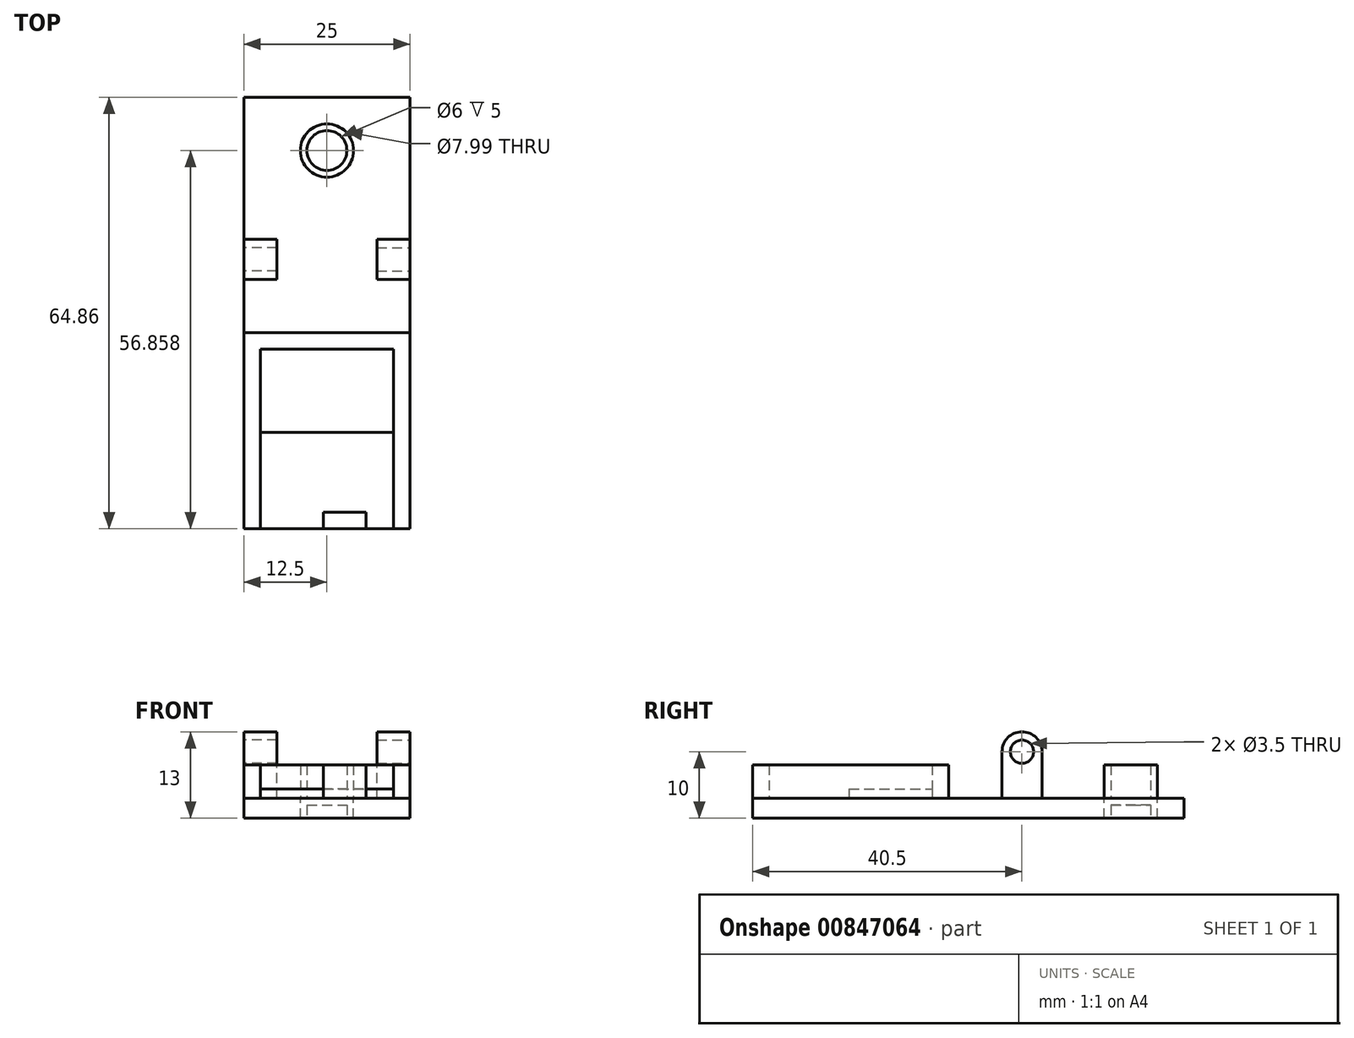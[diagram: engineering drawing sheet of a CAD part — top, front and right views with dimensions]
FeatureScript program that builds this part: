
annotation { "Feature Type Name" : "Feature", "Feature Type Description" : "" }
export const myFeature = defineFeature(function(context is Context, id is Id, definition is map)
    precondition{}
    {
        {
            var Q0;
            Q0=qCreatedBy(makeId("Top.planeOp"),FACE);
            var sketch = newSketch(context, id + "F0", { "sketchPlane" : qUnion([Q0])});
            skLineSegment(sketch, "E0.bottom", {"start": v(0, 0) * mm, "end": v(-20, 0) * mm});
            skLineSegment(sketch, "E0.top", {"start": v(0, 24.5) * mm, "end": v(-20, 24.5) * mm});
            skLineSegment(sketch, "E0.left", {"start": v(0, 0) * mm, "end": v(0, 24.5) * mm});
            skLineSegment(sketch, "E0.right", {"start": v(-20, 0) * mm, "end": v(-20, 24.5) * mm});
            skLineSegment(sketch, "E1.0", {"start": v(2.5, 27) * mm, "end": v(-22.5, 27) * mm});
            skLineSegment(sketch, "E1.1", {"start": v(2.5, -2.5) * mm, "end": v(2.5, 27) * mm});
            skLineSegment(sketch, "E1.2", {"start": v(2.5, -2.5) * mm, "end": v(-22.5, -2.5) * mm});
            skLineSegment(sketch, "E1.3", {"start": v(-22.5, -2.5) * mm, "end": v(-22.5, 27) * mm});
            skLineSegment(sketch, "E2.bottom", {"start": v(-20, 0) * mm, "end": v(-15.95, 0) * mm});
            skLineSegment(sketch, "E2.top", {"start": v(-20, -2.5) * mm, "end": v(-15.95, -2.5) * mm});
            skLineSegment(sketch, "E2.left", {"start": v(-20, 0) * mm, "end": v(-20, -2.5) * mm});
            skLineSegment(sketch, "E2.right", {"start": v(-15.95, 0) * mm, "end": v(-15.95, -2.5) * mm});
            skLineSegment(sketch, "E3.bottom", {"start": v(-4.14, 0) * mm, "end": v(0, 0) * mm});
            skLineSegment(sketch, "E3.top", {"start": v(-4.14, -2.5) * mm, "end": v(0, -2.5) * mm});
            skLineSegment(sketch, "E3.left", {"start": v(-4.14, 0) * mm, "end": v(-4.14, -2.5) * mm});
            skLineSegment(sketch, "E3.right", {"start": v(0, 0) * mm, "end": v(0, -2.5) * mm});
            skLineSegment(sketch, "E4.bottom", {"start": v(-20, 24.5) * mm, "end": v(0, 24.5) * mm});
            skLineSegment(sketch, "E4.top", {"start": v(-20, 12) * mm, "end": v(0, 12) * mm});
            skLineSegment(sketch, "E4.left", {"start": v(-20, 24.5) * mm, "end": v(-20, 12) * mm});
            skLineSegment(sketch, "E4.right", {"start": v(0, 24.5) * mm, "end": v(0, 12) * mm});
            skLineSegment(sketch, "E5.bottom", {"start": v(-10.54, 0) * mm, "end": v(-4.14, 0) * mm});
            skLineSegment(sketch, "E5.top", {"start": v(-10.54, -2.5) * mm, "end": v(-4.14, -2.5) * mm});
            skLineSegment(sketch, "E5.left", {"start": v(-10.54, 0) * mm, "end": v(-10.54, -2.5) * mm});
            skLineSegment(sketch, "E6.bottom", {"start": v(-22.5, 27) * mm, "end": v(2.5, 27) * mm});
            skLineSegment(sketch, "E6.top", {"start": v(-22.5, 62.36) * mm, "end": v(2.5, 62.36) * mm});
            skLineSegment(sketch, "E6.left", {"start": v(-22.5, 27) * mm, "end": v(-22.5, 62.36) * mm});
            skLineSegment(sketch, "E6.right", {"start": v(2.5, 27) * mm, "end": v(2.5, 62.36) * mm});
            skCircle(sketch, "E7", {"center": v(-10, 54.36) * mm, "radius": 3 * mm});
            skCircle(sketch, "E8", {"center": v(-10, 54.36) * mm, "radius": 4 * mm});
            skSolve(sketch);
        }
        {
            var Q0;
            {var subQ0=makeQuery(id+"F0.imprint","IMPRINT",EDGE,{"derivedFrom":sQuery(id+"F0.wireOp",EDGE,"E1.0")});var subQ2=sQuery(id+"F0.wireOp",EDGE,"E2.left");var subQ11=sQuery(id+"F0.wireOp",EDGE,"E0.top");var subQ17=makeQuery(id+"F0.imprint","IMPRINT",EDGE,{"derivedFrom":subQ2});var subQ19=sQuery(id+"F0.wireOp",EDGE,"E2.right");var subQ25=makeQuery(id+"F0.imprint","IMPRINT",EDGE,{"derivedFrom":subQ19});var subQ27=sQuery(id+"F0.wireOp",EDGE,"E3.left");var subQ29=makeQuery(id+"F0.imprint","IMPRINT",EDGE,{"derivedFrom":subQ27});Q0=qUnion([makeQuery(id+"F0.imprint","IMPRINT",FACE,{"disambiguationData":[TD([[subQ29,1.0]])]}),makeQuery(id+"F0.imprint","IMPRINT",FACE,{"disambiguationData":[TD([[subQ29,-1.0]])]}),makeQuery(id+"F0.imprint","IMPRINT",FACE,{"disambiguationData":[TD([[subQ17,1.0]])]}),makeQuery(id+"F0.imprint","IMPRINT",FACE,{"disambiguationData":[TD([[subQ25,1.0]])]}),makeQuery(id+"F0.imprint","IMPRINT",FACE,{"disambiguationData":[TD([[makeQuery(id+"F0.imprint","IMPRINT",EDGE,{"derivedFrom":subQ11}),-1.0]])]}),makeQuery(id+"F0.imprint","IMPRINT",FACE,{"disambiguationData":[TD([[subQ0,-1.0]])]})]);}
            var Q1;
            {var subQ0=sQuery(id+"F0.wireOp",EDGE,"E0.top");Q1=makeQuery(id+"F0.imprint","IMPRINT",FACE,{"disambiguationData":[TD([[makeQuery(id+"F0.imprint","IMPRINT",EDGE,{"derivedFrom":subQ0}),1.0]])]});}
            var Q2;
            {var subQ8=sQuery(id+"F0.wireOp",EDGE,"E4.top");Q2=makeQuery(id+"F0.imprint","IMPRINT",FACE,{"disambiguationData":[TD([[makeQuery(id+"F0.imprint","IMPRINT",EDGE,{"derivedFrom":subQ8}),-1.0]])]});}
            extrude(context, id + "F1", {"entities" : qUnion([Q0, Q1, Q2]), "oppositeDirection" : true, "depth" : 3 * mm, "offsetDistance" : 25 * mm});
        }
        {
            var Q0;
            {var subQ8=sQuery(id+"F0.wireOp",EDGE,"E0.top");Q0=makeQuery(id+"F0.imprint","IMPRINT",FACE,{"disambiguationData":[TD([[makeQuery(id+"F0.imprint","IMPRINT",EDGE,{"derivedFrom":subQ8}),-1.0]])]});}
            var Q1;
            {var subQ0=sQuery(id+"F0.wireOp",EDGE,"E3.left");Q1=makeQuery(id+"F0.imprint","IMPRINT",FACE,{"disambiguationData":[TD([[makeQuery(id+"F0.imprint","IMPRINT",EDGE,{"derivedFrom":subQ0}),-1.0]])]});}
            extrude(context, id + "F2", {"entities" : qUnion([Q0, Q1]), "depth" : 5 * mm, "offsetDistance" : 25 * mm});
        }
        {
            var Q0;
            {var subQ0=sQuery(id+"F0.wireOp",EDGE,"E0.top");Q0=makeQuery(id+"F0.imprint","IMPRINT",FACE,{"disambiguationData":[TD([[makeQuery(id+"F0.imprint","IMPRINT",EDGE,{"derivedFrom":subQ0}),1.0]])]});}
            extrude(context, id + "F3", {"entities" : qUnion([Q0]), "depth" : 1.4 * mm, "offsetDistance" : 25 * mm});
        }
        {
            var Q0;
            Q0=makeQuery(id+"F0.imprint","IMPRINT",FACE,{"disambiguationData":[TD([[makeQuery(id+"F0.imprint","IMPRINT",EDGE,{"derivedFrom":sQuery(id+"F0.wireOp",EDGE,"E7")}),-1.0]])]});
            extrude(context, id + "F4", {"entities" : qUnion([Q0]), "depth" : 5 * mm, "offsetDistance" : 25 * mm});
        }
        {
            var Q0;
            Q0=makeQuery(id+"F0.imprint","IMPRINT",FACE,{"disambiguationData":[TD([[makeQuery(id+"F0.imprint","IMPRINT",EDGE,{"derivedFrom":sQuery(id+"F0.wireOp",EDGE,"E7")}),1.0]])]});
            var Q1;
            Q1=makeQuery(id+"F0.imprint","IMPRINT",FACE,{"disambiguationData":[TD([[makeQuery(id+"F0.imprint","IMPRINT",EDGE,{"derivedFrom":sQuery(id+"F0.wireOp",EDGE,"E7")}),-1.0]])]});
            extrude(context, id + "F5", {"entities" : qUnion([Q0, Q1]), "oppositeDirection" : true, "depth" : 3 * mm, "offsetDistance" : 25 * mm});
        }
        {
            var Q0;
            Q0=makeQuery(id+"F1.opExtrude","SWEPT_FACE",FACE,{"disambiguationData":[OSD([sQuery(id+"F0.wireOp",EDGE,"E1.1"),sQuery(id+"F0.wireOp",EDGE,"E6.right")])]});
            var sketch = newSketch(context, id + "F6", { "sketchPlane" : qUnion([Q0])});
            skLineSegment(sketch, "E9.bottom", {"start": v(35, 0) * mm, "end": v(41, 0) * mm});
            skLineSegment(sketch, "E9.top", {"start": v(35, 7) * mm, "end": v(41, 7) * mm});
            skLineSegment(sketch, "E9.left", {"start": v(35, 0) * mm, "end": v(35, 7) * mm});
            skLineSegment(sketch, "E9.right", {"start": v(41, 0) * mm, "end": v(41, 7) * mm});
            skArc(sketch, "E10", {"start": v(41, 7) * mm, "mid": v(38, 10) * mm, "end": v(35, 7) * mm});
            skCircle(sketch, "E11", {"center": v(38, 7) * mm, "radius": 1.75 * mm});
            skSolve(sketch);
        }
        {
            var Q0;
            {var subQ0=sQuery(id+"F6.wireOp",EDGE,"E10");Q0=makeQuery(id+"F6.imprint","IMPRINT",FACE,{"disambiguationData":[TD([[makeQuery(id+"F6.imprint","IMPRINT",EDGE,{"derivedFrom":subQ0}),1.0]])]});}
            var Q1;
            Q1=makeQuery(id+"F6.imprint","IMPRINT",FACE,{"disambiguationData":[TD([[makeQuery(id+"F6.imprint","IMPRINT",EDGE,{"derivedFrom":sQuery(id+"F6.wireOp",EDGE,"E9.bottom")}),1.0]])]});
            extrude(context, id + "F7", {"entities" : qUnion([Q0, Q1]), "oppositeDirection" : true, "depth" : 5 * mm, "offsetDistance" : 25 * mm});
        }
        {
            var Q0;
            Q0=makeQuery(id+"F1.opExtrude","SWEPT_FACE",FACE,{"disambiguationData":[OSD([sQuery(id+"F0.wireOp",EDGE,"E1.3"),sQuery(id+"F0.wireOp",EDGE,"E6.left")])]});
            var sketch = newSketch(context, id + "F8", { "sketchPlane" : qUnion([Q0])});
            skLineSegment(sketch, "E12.bottom", {"start": v(-41, 0) * mm, "end": v(-35, 0) * mm});
            skLineSegment(sketch, "E12.top", {"start": v(-41, 7) * mm, "end": v(-35, 7) * mm});
            skLineSegment(sketch, "E12.left", {"start": v(-41, 0) * mm, "end": v(-41, 7) * mm});
            skLineSegment(sketch, "E12.right", {"start": v(-35, 0) * mm, "end": v(-35, 7) * mm});
            skArc(sketch, "E13", {"start": v(-35, 7) * mm, "mid": v(-38, 10) * mm, "end": v(-41, 7) * mm});
            skCircle(sketch, "E14", {"center": v(-38, 7) * mm, "radius": 1.75 * mm});
            skSolve(sketch);
        }
        {
            var Q0;
            Q0 = qSketchRegion(id + "F8", true);
            extrude(context, id + "F9", {"entities" : qUnion([Q0]), "operationType" : NewBodyOperationType.ADD, "oppositeDirection" : true, "depth" : 5 * mm, "offsetDistance" : 25 * mm});
        }
        {
            var Q0;
            Q0=makeQuery(id+"F1.opExtrude","CAP_FACE",FACE,{"disambiguationData":[OSD([sQuery(id+"F0.wireOp",EDGE,"E1.1"),sQuery(id+"F0.wireOp",EDGE,"E1.2"),sQuery(id+"F0.wireOp",EDGE,"E1.3"),sQuery(id+"F0.wireOp",EDGE,"E6.top"),sQuery(id+"F0.wireOp",EDGE,"E6.left"),sQuery(id+"F0.wireOp",EDGE,"E6.right"),sQuery(id+"F0.wireOp",EDGE,"E8")])],"isStart":false});
            var sketch = newSketch(context, id + "F10", { "sketchPlane" : qUnion([Q0])});
            skCircle(sketch, "E15", {"center": v(-10, -54.36) * mm, "radius": 3 * mm});
            skSolve(sketch);
        }
        {
            var Q0;
            Q0 = qSketchRegion(id + "F10", true);
            extrude(context, id + "F11", {"entities" : qUnion([Q0]), "oppositeDirection" : true, "depth" : 2 * mm, "offsetDistance" : 25 * mm});
        }
    });
